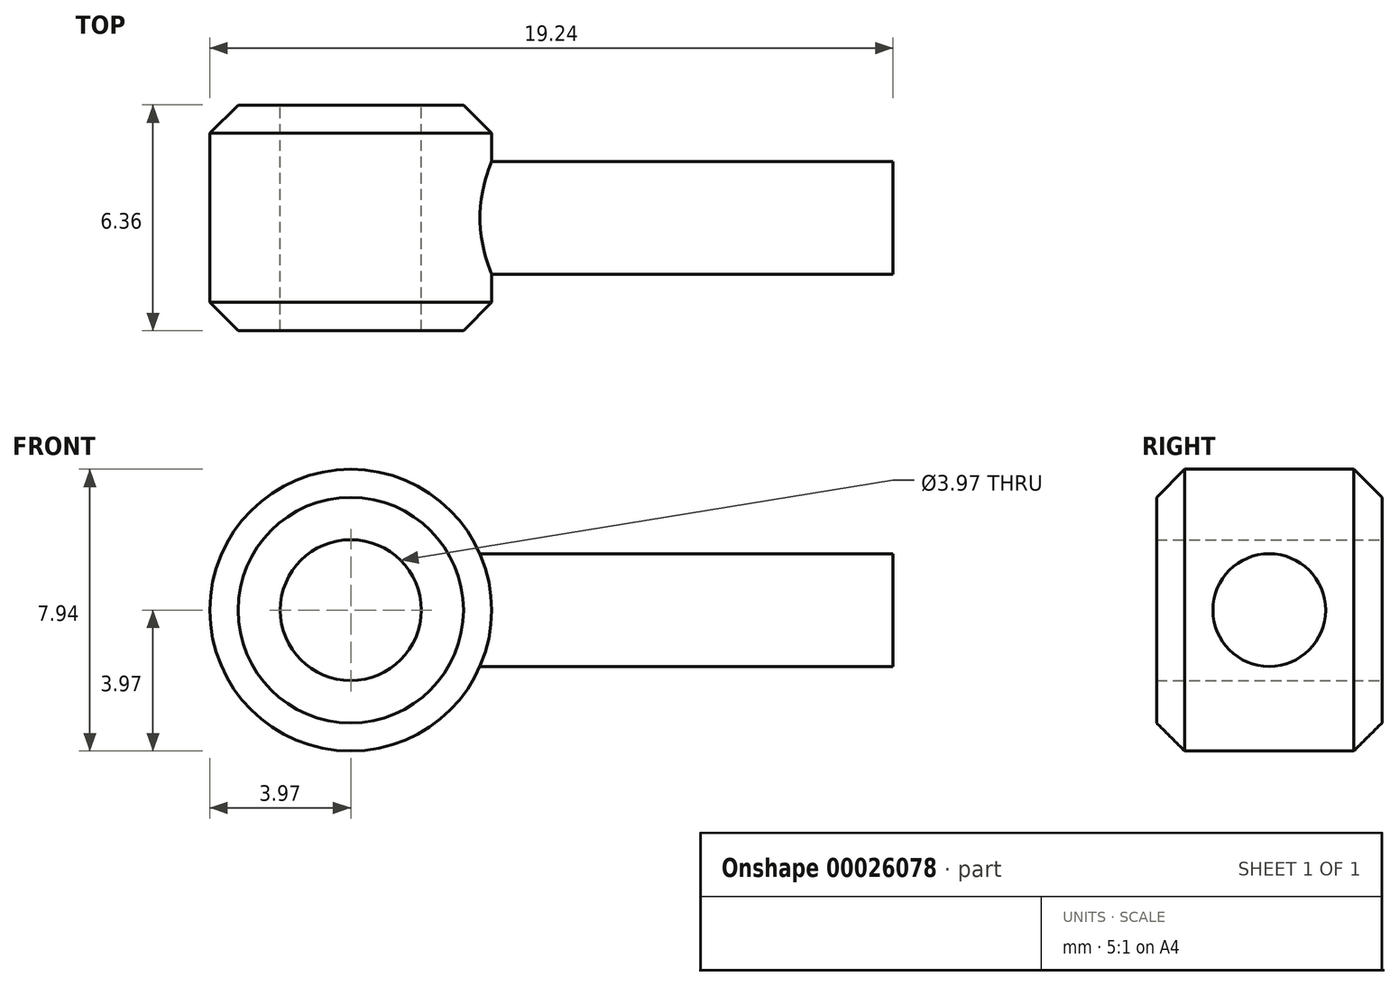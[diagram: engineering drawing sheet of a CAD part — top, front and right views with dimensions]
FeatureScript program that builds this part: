
annotation { "Feature Type Name" : "Feature", "Feature Type Description" : "" }
export const myFeature = defineFeature(function(context is Context, id is Id, definition is map)
    precondition{}
    {
        {
            var Q0;
            Q0=qCreatedBy(makeId("Front.planeOp"),FACE);
            var sketch = newSketch(context, id + "F0", { "sketchPlane" : qUnion([Q0])});
            skCircle(sketch, "E0", {"center": v(0, 0) * mm, "radius": 1.98 * mm});
            skCircle(sketch, "E1", {"center": v(0, 0) * mm, "radius": 3.97 * mm});
            skSolve(sketch);
        }
        {
            var Q0;
            Q0=qCreatedBy(makeId("Front.planeOp"),FACE);
            var sketch = newSketch(context, id + "F1", { "sketchPlane" : qUnion([Q0])});
            skArc(sketch, "E2.0", {"start": v(3.97, 0) * mm, "mid": v(3.89, 0.81) * mm, "end": v(3.64, 1.59) * mm});
            skLineSegment(sketch, "E3", {"start": v(3.64, 1.59) * mm, "end": v(15.27, 1.59) * mm});
            skLineSegment(sketch, "E4", {"start": v(15.27, 1.59) * mm, "end": v(15.27, 0) * mm});
            skLineSegment(sketch, "E5", {"start": v(15.27, 0) * mm, "end": v(3.97, 0) * mm});
            skSolve(sketch);
        }
        {
            var Q0;
            Q0=makeQuery(id+"F0.imprint","IMPRINT",FACE,{"disambiguationData":[TD([[makeQuery(id+"F0.imprint","IMPRINT",EDGE,{"derivedFrom":sQuery(id+"F0.wireOp",EDGE,"E0")}),-1.0]])]});
            extrude(context, id + "F2", {"entities" : qUnion([Q0]), "endBound" : BoundingType.SYMMETRIC, "depth" : 6.35 * mm});
        }
        {
            var Q0;
            Q0=makeQuery(id+"F1.imprint","IMPRINT",FACE,{"disambiguationData":[TD([[makeQuery(id+"F1.imprint","IMPRINT",EDGE,{"derivedFrom":sQuery(id+"F1.wireOp",EDGE,"E2.0")}),-1.0]])]});
            var Q1;
            Q1=sQuery(id+"F1.wireOp",EDGE,"E5");
            revolve(context, id + "F3", {"operationType" : NewBodyOperationType.ADD, "entities" : qUnion([Q0]), "axis" : qUnion([Q1]), "revolveType" : RevolveType.FULL});
        }
        {
            var Q0;
            Q0=makeQuery(id+"F2.opExtrude","CAP_EDGE",EDGE,{"disambiguationData":[OSD([sQuery(id+"F0.wireOp",EDGE,"E1")])],"isStart":false});
            var Q1;
            Q1=makeQuery(id+"F2.opExtrude","CAP_EDGE",EDGE,{"disambiguationData":[OSD([sQuery(id+"F0.wireOp",EDGE,"E1")])],"isStart":true});
            chamfer(context, id + "F4", {"entities" : qUnion([Q0, Q1]), "width" : 0.8 * mm, "tangentPropagation" : true});
        }
    });
